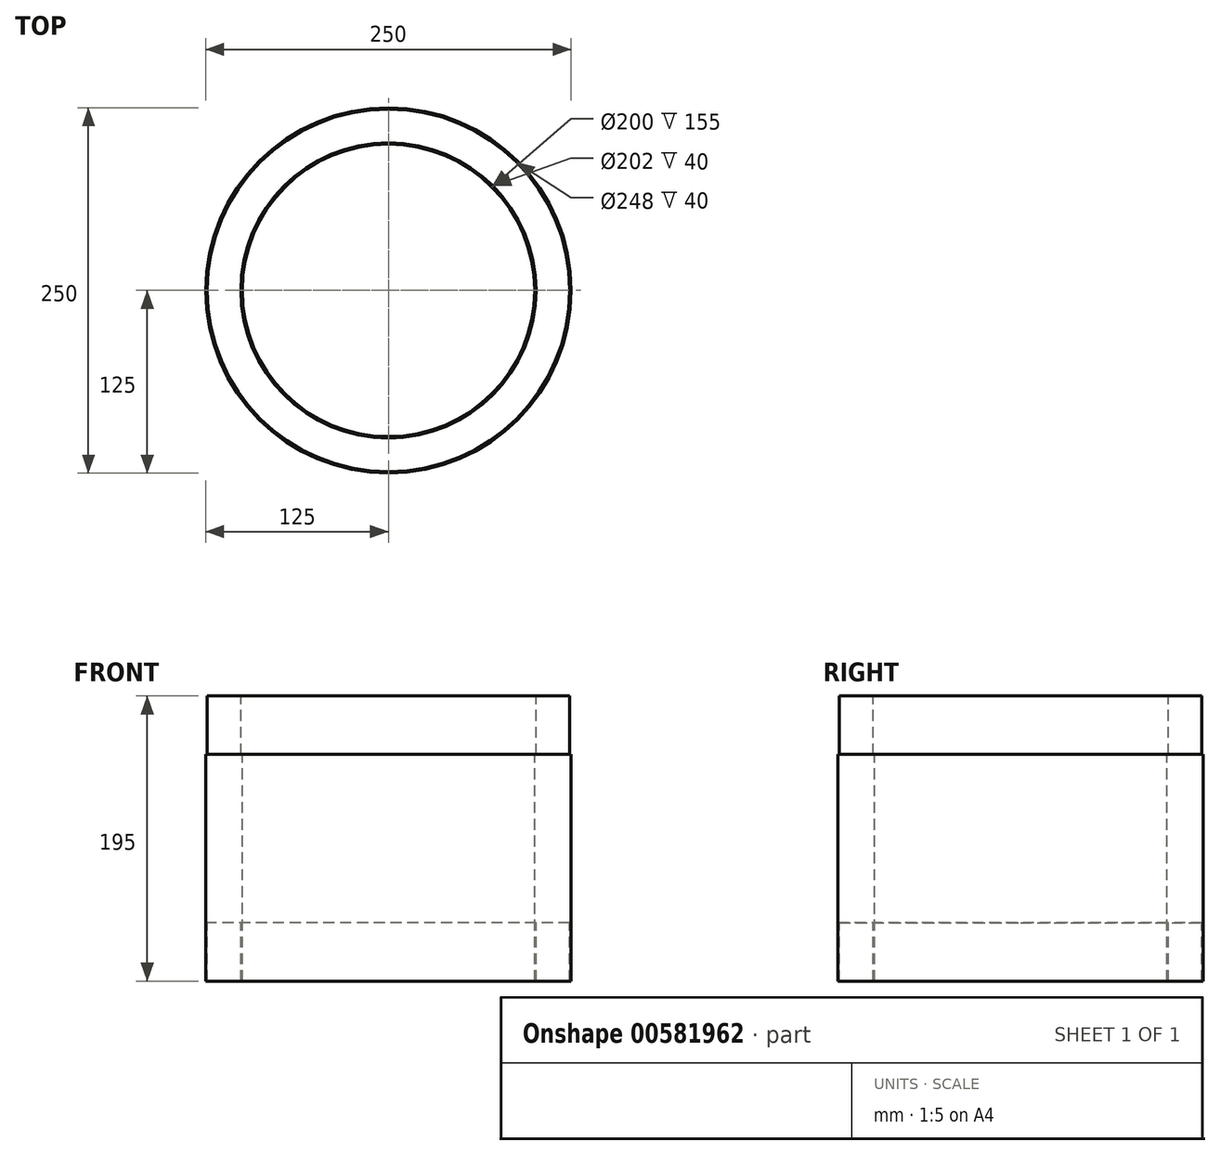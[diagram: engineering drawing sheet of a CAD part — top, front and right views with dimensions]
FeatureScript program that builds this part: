
annotation { "Feature Type Name" : "Feature", "Feature Type Description" : "" }
export const myFeature = defineFeature(function(context is Context, id is Id, definition is map)
    precondition{}
    {
        {
            var Q0;
            Q0=qCreatedBy(makeId("Front.planeOp"),FACE);
            var sketch = newSketch(context, id + "F0", { "sketchPlane" : qUnion([Q0])});
            skLineSegment(sketch, "E0", {"start": v(0, 345.75) * mm, "end": v(0, -558.03) * mm, "construction": true});
            skLineSegment(sketch, "E1", {"start": v(-100, -518.84) * mm, "end": v(-100, -363.84) * mm});
            skLineSegment(sketch, "E2", {"start": v(-100, -363.84) * mm, "end": v(-101, -363.84) * mm});
            skLineSegment(sketch, "E3", {"start": v(-101, -363.84) * mm, "end": v(-101, -323.84) * mm});
            skLineSegment(sketch, "E4", {"start": v(-101, -323.84) * mm, "end": v(-124, -323.84) * mm});
            skLineSegment(sketch, "E5", {"start": v(-124, -323.84) * mm, "end": v(-124, -363.84) * mm});
            skLineSegment(sketch, "E6", {"start": v(-124, -363.84) * mm, "end": v(-125, -363.84) * mm});
            skLineSegment(sketch, "E7", {"start": v(-125, -363.84) * mm, "end": v(-125, -518.84) * mm});
            skLineSegment(sketch, "E8", {"start": v(-125, -518.84) * mm, "end": v(-124, -518.84) * mm});
            skLineSegment(sketch, "E9", {"start": v(-124, -518.84) * mm, "end": v(-124, -478.84) * mm});
            skLineSegment(sketch, "E10", {"start": v(-124, -478.84) * mm, "end": v(-101, -478.84) * mm});
            skLineSegment(sketch, "E11", {"start": v(-101, -478.84) * mm, "end": v(-101, -518.84) * mm});
            skLineSegment(sketch, "E12", {"start": v(-101, -518.84) * mm, "end": v(-100, -518.84) * mm});
            skSolve(sketch);
        }
        {
            var Q0;
            Q0=qSketchRegion(id+"F0",true);
            var Q1;
            Q1=sQuery(id+"F0.wireOp",EDGE,"E0");
            revolve(context, id + "F1", {"entities" : qUnion([Q0]), "axis" : qUnion([Q1]), "revolveType" : RevolveType.FULL});
        }
    });
